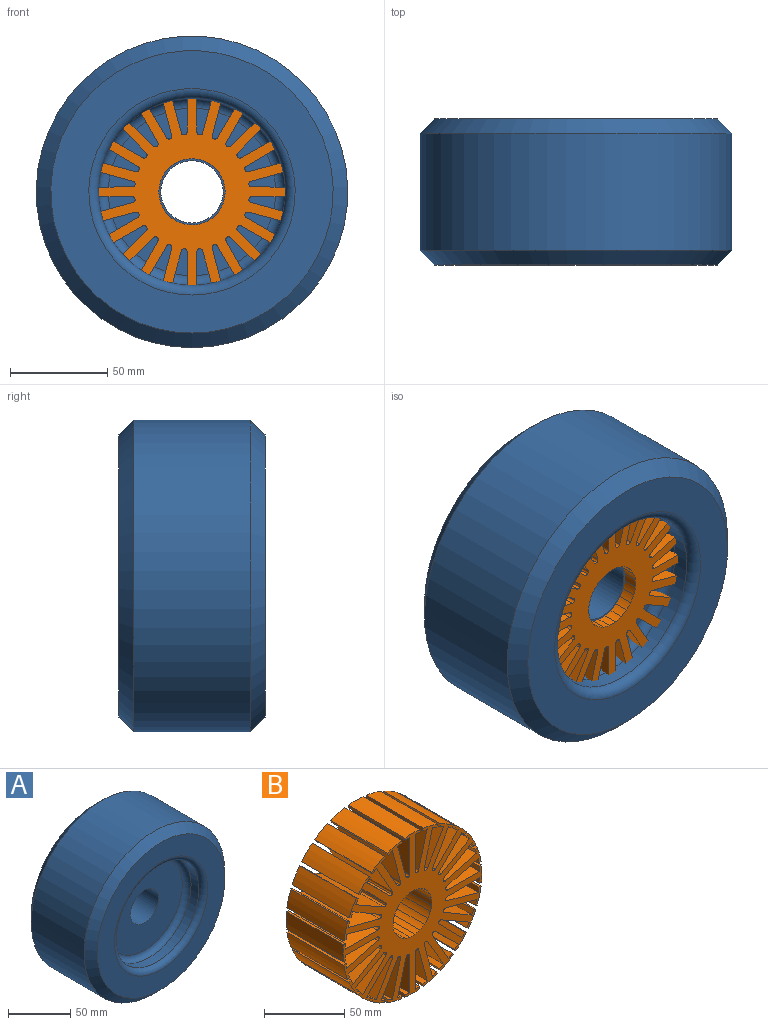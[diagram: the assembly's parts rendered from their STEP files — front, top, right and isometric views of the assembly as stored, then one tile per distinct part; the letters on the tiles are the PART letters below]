
ASSEMBLY  parts=2 mates=1
PART A: 14 faces, bbox 160x75x160 mm
  f0: cylinder r=16mm len=37.5mm, axis (0,1,0), area 3769.9mm2, adj f1,f2
  f1: plane 86x86mm, normal (0,-1,0), area 5004.6mm2, adj f0,f10
  f2: plane 86x86mm, normal (0,1,0), area 5004.6mm2, adj f0,f13
  f3: cylinder r=48mm len=96mm, axis (0,1,0), area 2638.9mm2, adj f10,f12
  f4: cylinder r=48mm len=96mm, axis (0,1,0), area 2638.9mm2, adj f11,f13
  f5: cylinder r=80mm len=160mm, axis (0,1,0), area 30159.3mm2, adj f8,f9
  f6: plane 145x145mm, normal (0,-1,0), area 7688.3mm2, adj f8,f12
  f7: plane 145x145mm, normal (0,1,0), area 7688.3mm2, adj f9,f11
  f8: cone r=72.5mm half-angle=45deg, axis (0,1,0), area 5081.5mm2, adj f5,f6
  f9: cone r=80mm half-angle=45deg, axis (0,-1,0), area 5081.5mm2, adj f5,f7
  f10: torus R=43mm, axis (0,-1,0), area 2279mm2, adj f1,f3
  f11: torus R=53mm, axis (0,-1,0), area 2458.4mm2, adj f4,f7
  f12: torus R=53mm, axis (0,-1,0), area 2458.4mm2, adj f3,f6
  f13: torus R=43mm, axis (0,-1,0), area 2279mm2, adj f2,f4
PART B: 250 faces, bbox 122x50x122 mm
  f0: cylinder r=1.5mm len=50mm, axis (0,1,0), area 108.3mm2, adj f10,f12,f13,f150
  f1: cylinder r=17mm len=50mm, axis (0,1,0), area 222.5mm2, adj f11,f12,f13,f147
  f2: plane 50x0mm, normal (0.99,0,-0.13), area 0mm2, adj f3,f12,f13,f14
  f3: cylinder r=1.5mm len=50mm, axis (0,1,0), area 108.3mm2, adj f2,f4,f12,f13
  f4: plane 50x28.48mm, normal (1,0,0), area 1424.1mm2, adj f3,f5,f12,f13
  f5: plane 50x3.93mm, normal (-0.13,0,-0.99), area 198.3mm2, adj f4,f6,f12,f13
  f6: plane 50x1.98mm, normal (0.99,0,-0.13), area 100mm2, adj f5,f7,f12,f13
  f7: cylinder r=61.01mm len=50mm, axis (0,1,0), area 660.6mm2, adj f6,f8,f12,f13
  f8: plane 50x1.98mm, normal (-0.99,0,-0.13), area 100mm2, adj f7,f9,f12,f13
  f9: plane 50x3.93mm, normal (0.13,0,-0.99), area 198.2mm2, adj f8,f10,f12,f13
  f10: plane 50x28.48mm, normal (-1,0,0), area 1424.1mm2, adj f0,f9,f12,f13
  f11: plane 50x0mm, normal (-0.99,0,-0.13), area 0mm2, adj f1,f12,f13,f149
  f12: plane 122.03x122.03mm, normal (0,-1,0), area 5955.8mm2, adj f0,f1,f2,f3,f4,f5,f6,f7
  f13: plane 122.03x122.03mm, normal (0,1,0), area 5955.8mm2, adj f0,f1,f2,f3,f4,f5,f6,f7
  f14: cylinder r=1.5mm len=50mm, axis (0,1,0), area 108.3mm2, adj f2,f12,f13,f146
  f15: cylinder r=1.5mm len=50mm, axis (0,1,0), area 108.3mm2, adj f12,f13,f25,f28
  f16: cylinder r=17mm len=50mm, axis (0,1,0), area 222.5mm2, adj f12,f13,f26,f249
  f17: plane 50x0mm, normal (-0.92,0,0.38), area 0mm2, adj f12,f13,f18,f148
  f18: cylinder r=1.5mm len=50mm, axis (0,1,0), area 108.3mm2, adj f12,f13,f17,f19
  f19: plane 50x27.55mm, normal (-0.97,0,0.25), area 1424.1mm2, adj f12,f13,f18,f20
  f20: plane 50x3.66mm, normal (0.38,0,0.92), area 198.2mm2, adj f12,f13,f19,f21
  f21: plane 50x1.85mm, normal (-0.92,0,0.38), area 100mm2, adj f12,f13,f20,f22
  f22: cylinder r=61.01mm len=50mm, axis (0,1,0), area 660.6mm2, adj f12,f13,f21,f23
  f23: plane 50x1.98mm, normal (0.99,0,-0.13), area 100mm2, adj f12,f13,f22,f24
  f24: plane 50x3.93mm, normal (0.13,0,0.99), area 198.3mm2, adj f12,f13,f23,f25
  f25: plane 50x27.48mm, normal (0.96,0,-0.26), area 1424.1mm2, adj f12,f13,f15,f24
  f26: plane 50x0mm, normal (0.99,0,-0.13), area 0mm2, adj f12,f13,f16,f27
  f27: cylinder r=17mm len=50mm, axis (0,1,0), area 222.5mm2, adj f12,f13,f26,f38
  f28: plane 50x0mm, normal (-0.99,0,0.13), area 0mm2, adj f12,f13,f15,f29
  f29: cylinder r=1.5mm len=50mm, axis (0,1,0), area 108.3mm2, adj f12,f13,f28,f30
  f30: plane 50x28.48mm, normal (-1,0,0), area 1424.1mm2, adj f12,f13,f29,f31
  f31: plane 50x3.93mm, normal (0.13,0,0.99), area 198.3mm2, adj f12,f13,f30,f32
  f32: plane 50x1.98mm, normal (-0.99,0,0.13), area 100mm2, adj f12,f13,f31,f33
  f33: cylinder r=61.01mm len=50mm, axis (0,1,0), area 660.6mm2, adj f12,f13,f32,f34
  f34: plane 50x1.98mm, normal (0.99,0,0.13), area 100mm2, adj f12,f13,f33,f35
  f35: plane 50x3.93mm, normal (-0.13,0,0.99), area 198.3mm2, adj f12,f13,f34,f36
  f36: plane 50x28.48mm, normal (1,0,0), area 1424.1mm2, adj f12,f13,f35,f37
  f37: cylinder r=1.5mm len=50mm, axis (0,1,0), area 108.3mm2, adj f12,f13,f36,f39
  f38: cylinder r=17mm len=50mm, axis (0,1,0), area 222.5mm2, adj f12,f13,f27,f48
  f39: cylinder r=1.5mm len=50mm, axis (0,1,0), area 108.3mm2, adj f12,f13,f37,f40
  f40: plane 50x27.47mm, normal (-0.96,0,-0.26), area 1424.1mm2, adj f12,f13,f39,f41
  f41: plane 50x3.93mm, normal (-0.13,0,0.99), area 198.3mm2, adj f12,f13,f40,f42
  f42: plane 50x1.98mm, normal (-0.99,0,-0.13), area 100mm2, adj f12,f13,f41,f43
  f43: cylinder r=61.01mm len=50mm, axis (0,1,0), area 660.6mm2, adj f12,f13,f42,f44
  f44: plane 50x1.85mm, normal (0.92,0,0.38), area 100mm2, adj f12,f13,f43,f45
  f45: plane 50x3.66mm, normal (-0.38,0,0.92), area 198.3mm2, adj f12,f13,f44,f46
  f46: plane 50x27.55mm, normal (0.97,0,0.25), area 1424.1mm2, adj f12,f13,f45,f47
  f47: cylinder r=1.5mm len=50mm, axis (0,1,0), area 108.3mm2, adj f12,f13,f46,f49
  f48: cylinder r=17mm len=50mm, axis (0,1,0), area 222.5mm2, adj f12,f13,f38,f58
  f49: cylinder r=1.5mm len=50mm, axis (0,1,0), area 108.3mm2, adj f12,f13,f47,f50
  f50: plane 50x24.6mm, normal (-0.86,0,-0.5), area 1424.1mm2, adj f12,f13,f49,f51
  f51: plane 50x3.66mm, normal (-0.38,0,0.92), area 198.2mm2, adj f12,f13,f50,f52
  f52: plane 50x1.85mm, normal (-0.92,0,-0.38), area 100mm2, adj f12,f13,f51,f53
  f53: cylinder r=61.01mm len=50mm, axis (0,1,0), area 660.6mm2, adj f12,f13,f52,f54
  f54: plane 50x1.59mm, normal (0.79,0,0.61), area 100mm2, adj f12,f13,f53,f55
  f55: plane 50x3.15mm, normal (-0.61,0,0.79), area 198.2mm2, adj f12,f13,f54,f56
  f56: plane 50x24.74mm, normal (0.87,0,0.5), area 1424.1mm2, adj f12,f13,f55,f57
  f57: cylinder r=1.5mm len=50mm, axis (0,1,0), area 108.3mm2, adj f12,f13,f56,f59
  f58: cylinder r=17mm len=50mm, axis (0,1,0), area 222.5mm2, adj f12,f13,f48,f68
  f59: cylinder r=1.5mm len=50mm, axis (0,1,0), area 108.3mm2, adj f12,f13,f57,f60
  f60: plane 50x20.24mm, normal (-0.7,0,-0.71), area 1424.1mm2, adj f12,f13,f59,f61
  f61: plane 50x3.15mm, normal (-0.61,0,0.79), area 198.3mm2, adj f12,f13,f60,f62
  f62: plane 50x1.59mm, normal (-0.79,0,-0.61), area 100mm2, adj f12,f13,f61,f63
  f63: cylinder r=61.01mm len=50mm, axis (0,1,0), area 660.6mm2, adj f12,f13,f62,f64
  f64: plane 50x1.59mm, normal (0.61,0,0.79), area 100mm2, adj f12,f13,f63,f65
  f65: plane 50x3.15mm, normal (-0.79,0,0.61), area 198.2mm2, adj f12,f13,f64,f66
  f66: plane 50x20.24mm, normal (0.71,0,0.7), area 1424.1mm2, adj f12,f13,f65,f67
  f67: cylinder r=1.5mm len=50mm, axis (0,1,0), area 108.3mm2, adj f12,f13,f66,f69
  f68: cylinder r=17mm len=50mm, axis (0,1,0), area 222.5mm2, adj f12,f13,f58,f78
  f69: cylinder r=1.5mm len=50mm, axis (0,1,0), area 108.3mm2, adj f12,f13,f67,f70
  f70: plane 50x24.74mm, normal (-0.5,0,-0.87), area 1424.1mm2, adj f12,f13,f69,f71
  f71: plane 50x3.15mm, normal (-0.79,0,0.61), area 198.3mm2, adj f12,f13,f70,f72
  f72: plane 50x1.59mm, normal (-0.61,0,-0.79), area 100mm2, adj f12,f13,f71,f73
  f73: cylinder r=61.01mm len=50mm, axis (0,1,0), area 660.6mm2, adj f12,f13,f72,f74
  f74: plane 50x1.85mm, normal (0.38,0,0.92), area 100mm2, adj f12,f13,f73,f75
  f75: plane 50x3.66mm, normal (-0.92,0,0.38), area 198.2mm2, adj f12,f13,f74,f76
  f76: plane 50x24.6mm, normal (0.5,0,0.86), area 1424.1mm2, adj f12,f13,f75,f77
  f77: cylinder r=1.5mm len=50mm, axis (0,1,0), area 108.3mm2, adj f12,f13,f76,f79
  f78: cylinder r=17mm len=50mm, axis (0,1,0), area 222.5mm2, adj f12,f13,f68,f88
  f79: cylinder r=1.5mm len=50mm, axis (0,1,0), area 108.3mm2, adj f12,f13,f77,f80
  f80: plane 50x27.55mm, normal (-0.25,0,-0.97), area 1424.1mm2, adj f12,f13,f79,f81
  f81: plane 50x3.66mm, normal (-0.92,0,0.38), area 198.2mm2, adj f12,f13,f80,f82
  f82: plane 50x1.85mm, normal (-0.38,0,-0.92), area 100mm2, adj f12,f13,f81,f83
  f83: cylinder r=61.01mm len=50mm, axis (0,1,0), area 660.6mm2, adj f12,f13,f82,f84
  f84: plane 50x1.98mm, normal (0.13,0,0.99), area 100mm2, adj f12,f13,f83,f85
  f85: plane 50x3.93mm, normal (-0.99,0,0.13), area 198.2mm2, adj f12,f13,f84,f86
  f86: plane 50x27.48mm, normal (0.26,0,0.96), area 1424.1mm2, adj f12,f13,f85,f87
  f87: cylinder r=1.5mm len=50mm, axis (0,1,0), area 108.3mm2, adj f12,f13,f86,f89
  f88: cylinder r=17mm len=50mm, axis (0,1,0), area 222.5mm2, adj f12,f13,f78,f98
  f89: cylinder r=1.5mm len=50mm, axis (0,1,0), area 108.3mm2, adj f12,f13,f87,f90
  f90: plane 50x28.48mm, normal (0,0,-1), area 1424.1mm2, adj f12,f13,f89,f91
  f91: plane 50x3.93mm, normal (-0.99,0,0.13), area 198.3mm2, adj f12,f13,f90,f92
  f92: plane 50x1.98mm, normal (-0.13,0,-0.99), area 100mm2, adj f12,f13,f91,f93
  f93: cylinder r=61.01mm len=50mm, axis (0,1,0), area 660.6mm2, adj f12,f13,f92,f94
  f94: plane 50x1.98mm, normal (-0.13,0,0.99), area 100mm2, adj f12,f13,f93,f95
  f95: plane 50x3.93mm, normal (-0.99,0,-0.13), area 198.3mm2, adj f12,f13,f94,f96
  f96: plane 50x28.48mm, normal (0,0,1), area 1424.1mm2, adj f12,f13,f95,f97
  f97: cylinder r=1.5mm len=50mm, axis (0,1,0), area 108.3mm2, adj f12,f13,f96,f99
  f98: cylinder r=17mm len=50mm, axis (0,1,0), area 222.5mm2, adj f12,f13,f88,f108
  f99: cylinder r=1.5mm len=50mm, axis (0,1,0), area 108.3mm2, adj f12,f13,f97,f100
  f100: plane 50x27.47mm, normal (0.26,0,-0.96), area 1424.1mm2, adj f12,f13,f99,f101
  f101: plane 50x3.93mm, normal (-0.99,0,-0.13), area 198.2mm2, adj f12,f13,f100,f102
  f102: plane 50x1.98mm, normal (0.13,0,-0.99), area 100mm2, adj f12,f13,f101,f103
  f103: cylinder r=61.01mm len=50mm, axis (0,1,0), area 660.6mm2, adj f12,f13,f102,f104
  f104: plane 50x1.85mm, normal (-0.38,0,0.92), area 100mm2, adj f12,f13,f103,f105
  f105: plane 50x3.66mm, normal (-0.92,0,-0.38), area 198.3mm2, adj f12,f13,f104,f106
  f106: plane 50x27.55mm, normal (-0.25,0,0.97), area 1424.1mm2, adj f12,f13,f105,f107
  f107: cylinder r=1.5mm len=50mm, axis (0,1,0), area 108.3mm2, adj f12,f13,f106,f109
  f108: cylinder r=17mm len=50mm, axis (0,1,0), area 222.5mm2, adj f12,f13,f98,f118
  f109: cylinder r=1.5mm len=50mm, axis (0,1,0), area 108.3mm2, adj f12,f13,f107,f110
  f110: plane 50x24.6mm, normal (0.5,0,-0.86), area 1424.1mm2, adj f12,f13,f109,f111
  f111: plane 50x3.66mm, normal (-0.92,0,-0.38), area 198.3mm2, adj f12,f13,f110,f112
  f112: plane 50x1.85mm, normal (0.38,0,-0.92), area 100mm2, adj f12,f13,f111,f113
  f113: cylinder r=61.01mm len=50mm, axis (0,1,0), area 660.6mm2, adj f12,f13,f112,f114
  f114: plane 50x1.59mm, normal (-0.61,0,0.79), area 100mm2, adj f12,f13,f113,f115
  f115: plane 50x3.15mm, normal (-0.79,0,-0.61), area 198.2mm2, adj f12,f13,f114,f116
  f116: plane 50x24.74mm, normal (-0.5,0,0.87), area 1424.1mm2, adj f12,f13,f115,f117
  f117: cylinder r=1.5mm len=50mm, axis (0,1,0), area 108.3mm2, adj f12,f13,f116,f119
  f118: cylinder r=17mm len=50mm, axis (0,1,0), area 222.5mm2, adj f12,f13,f108,f128
  f119: cylinder r=1.5mm len=50mm, axis (0,1,0), area 108.3mm2, adj f12,f13,f117,f120
  f120: plane 50x20.24mm, normal (0.71,0,-0.7), area 1424.1mm2, adj f12,f13,f119,f121
  f121: plane 50x3.15mm, normal (-0.79,0,-0.61), area 198.3mm2, adj f12,f13,f120,f122
  f122: plane 50x1.59mm, normal (0.61,0,-0.79), area 100mm2, adj f12,f13,f121,f123
  f123: cylinder r=61.01mm len=50mm, axis (0,1,0), area 660.6mm2, adj f12,f13,f122,f124
  f124: plane 50x1.59mm, normal (-0.79,0,0.61), area 100mm2, adj f12,f13,f123,f125
  f125: plane 50x3.15mm, normal (-0.61,0,-0.79), area 198.2mm2, adj f12,f13,f124,f126
  f126: plane 50x20.24mm, normal (-0.7,0,0.71), area 1424.1mm2, adj f12,f13,f125,f127
  f127: cylinder r=1.5mm len=50mm, axis (0,1,0), area 108.3mm2, adj f12,f13,f126,f129
  f128: cylinder r=17mm len=50mm, axis (0,1,0), area 222.5mm2, adj f12,f13,f118,f138
  f129: cylinder r=1.5mm len=50mm, axis (0,1,0), area 108.3mm2, adj f12,f13,f127,f130
  f130: plane 50x24.74mm, normal (0.87,0,-0.5), area 1424.1mm2, adj f12,f13,f129,f131
  f131: plane 50x3.15mm, normal (-0.61,0,-0.79), area 198.2mm2, adj f12,f13,f130,f132
  f132: plane 50x1.59mm, normal (0.79,0,-0.61), area 100mm2, adj f12,f13,f131,f133
  f133: cylinder r=61.01mm len=50mm, axis (0,1,0), area 660.6mm2, adj f12,f13,f132,f134
  f134: plane 50x1.85mm, normal (-0.92,0,0.38), area 100mm2, adj f12,f13,f133,f135
  f135: plane 50x3.66mm, normal (-0.38,0,-0.92), area 198.2mm2, adj f12,f13,f134,f136
  f136: plane 50x24.6mm, normal (-0.86,0,0.5), area 1424.1mm2, adj f12,f13,f135,f137
  f137: cylinder r=1.5mm len=50mm, axis (0,1,0), area 108.3mm2, adj f12,f13,f136,f139
  f138: cylinder r=17mm len=50mm, axis (0,1,0), area 222.5mm2, adj f12,f13,f128,f147
  f139: cylinder r=1.5mm len=50mm, axis (0,1,0), area 108.3mm2, adj f12,f13,f137,f140
  f140: plane 50x27.55mm, normal (0.97,0,-0.25), area 1424.1mm2, adj f12,f13,f139,f141
  f141: plane 50x3.66mm, normal (-0.38,0,-0.92), area 198.3mm2, adj f12,f13,f140,f142
  f142: plane 50x1.85mm, normal (0.92,0,-0.38), area 100mm2, adj f12,f13,f141,f143
  f143: cylinder r=61.01mm len=50mm, axis (0,1,0), area 660.6mm2, adj f12,f13,f142,f144
  f144: plane 50x1.98mm, normal (-0.99,0,0.13), area 100mm2, adj f12,f13,f143,f145
  f145: plane 50x3.93mm, normal (-0.13,0,-0.99), area 198.3mm2, adj f12,f13,f144,f146
  f146: plane 50x27.48mm, normal (-0.96,0,0.26), area 1424.1mm2, adj f12,f13,f14,f145
  f147: plane 50x0mm, normal (-0.99,0,0.13), area 0mm2, adj f1,f12,f13,f138
  f148: cylinder r=1.5mm len=50mm, axis (0,1,0), area 108.3mm2, adj f12,f13,f17,f248
  f149: cylinder r=17mm len=50mm, axis (0,1,0), area 222.5mm2, adj f11,f12,f13,f170
  f150: plane 50x0mm, normal (0.99,0,0.13), area 0mm2, adj f0,f12,f13,f151
  f151: cylinder r=1.5mm len=50mm, axis (0,1,0), area 108.3mm2, adj f12,f13,f150,f152
  f152: plane 50x27.47mm, normal (0.96,0,0.26), area 1424.1mm2, adj f12,f13,f151,f153
  f153: plane 50x3.93mm, normal (0.13,0,-0.99), area 198.3mm2, adj f12,f13,f152,f154
  f154: plane 50x1.98mm, normal (0.99,0,0.13), area 100mm2, adj f12,f13,f153,f155
  f155: cylinder r=61.01mm len=50mm, axis (0,1,0), area 660.6mm2, adj f12,f13,f154,f156
  f156: plane 50x1.85mm, normal (-0.92,0,-0.38), area 100mm2, adj f12,f13,f155,f157
  f157: plane 50x3.66mm, normal (0.38,0,-0.92), area 198.2mm2, adj f12,f13,f156,f158
  f158: plane 50x27.55mm, normal (-0.97,0,-0.25), area 1424.1mm2, adj f12,f13,f157,f159
  f159: cylinder r=1.5mm len=50mm, axis (0,1,0), area 108.3mm2, adj f12,f13,f158,f171
  f160: cylinder r=17mm len=50mm, axis (0,1,0), area 222.5mm2, adj f12,f13,f170,f180
  f161: cylinder r=1.5mm len=50mm, axis (0,1,0), area 108.3mm2, adj f12,f13,f162,f179
  f162: plane 50x20.24mm, normal (0.7,0,0.71), area 1424.1mm2, adj f12,f13,f161,f163
  f163: plane 50x3.15mm, normal (0.61,0,-0.79), area 198.2mm2, adj f12,f13,f162,f164
  f164: plane 50x1.59mm, normal (0.79,0,0.61), area 100mm2, adj f12,f13,f163,f165
  f165: cylinder r=61.01mm len=50mm, axis (0,1,0), area 660.6mm2, adj f12,f13,f164,f166
  f166: plane 50x1.59mm, normal (-0.61,0,-0.79), area 100mm2, adj f12,f13,f165,f167
  f167: plane 50x3.15mm, normal (0.79,0,-0.61), area 198.2mm2, adj f12,f13,f166,f168
  f168: plane 50x20.24mm, normal (-0.71,0,-0.7), area 1424.1mm2, adj f12,f13,f167,f169
  f169: cylinder r=1.5mm len=50mm, axis (0,1,0), area 108.3mm2, adj f12,f13,f168,f181
  f170: cylinder r=17mm len=50mm, axis (0,1,0), area 222.5mm2, adj f12,f13,f149,f160
  f171: cylinder r=1.5mm len=50mm, axis (0,1,0), area 108.3mm2, adj f12,f13,f159,f172
  f172: plane 50x24.6mm, normal (0.86,0,0.5), area 1424.1mm2, adj f12,f13,f171,f173
  f173: plane 50x3.66mm, normal (0.38,0,-0.92), area 198.3mm2, adj f12,f13,f172,f174
  f174: plane 50x1.85mm, normal (0.92,0,0.38), area 100mm2, adj f12,f13,f173,f175
  f175: cylinder r=61.01mm len=50mm, axis (0,1,0), area 660.6mm2, adj f12,f13,f174,f176
  f176: plane 50x1.59mm, normal (-0.79,0,-0.61), area 100mm2, adj f12,f13,f175,f177
  f177: plane 50x3.15mm, normal (0.61,0,-0.79), area 198.2mm2, adj f12,f13,f176,f178
  f178: plane 50x24.74mm, normal (-0.87,0,-0.5), area 1424.1mm2, adj f12,f13,f177,f179
  f179: cylinder r=1.5mm len=50mm, axis (0,1,0), area 108.3mm2, adj f12,f13,f161,f178
  f180: cylinder r=17mm len=50mm, axis (0,1,0), area 222.5mm2, adj f12,f13,f160,f190
  f181: cylinder r=1.5mm len=50mm, axis (0,1,0), area 108.3mm2, adj f12,f13,f169,f182
  f182: plane 50x24.74mm, normal (0.5,0,0.87), area 1424.1mm2, adj f12,f13,f181,f183
  f183: plane 50x3.15mm, normal (0.79,0,-0.61), area 198.2mm2, adj f12,f13,f182,f184
  f184: plane 50x1.59mm, normal (0.61,0,0.79), area 100mm2, adj f12,f13,f183,f185
  f185: cylinder r=61.01mm len=50mm, axis (0,1,0), area 660.6mm2, adj f12,f13,f184,f186
  f186: plane 50x1.85mm, normal (-0.38,0,-0.92), area 100mm2, adj f12,f13,f185,f187
  f187: plane 50x3.66mm, normal (0.92,0,-0.38), area 198.3mm2, adj f12,f13,f186,f188
  f188: plane 50x24.6mm, normal (-0.5,0,-0.86), area 1424.1mm2, adj f12,f13,f187,f189
  f189: cylinder r=1.5mm len=50mm, axis (0,1,0), area 108.3mm2, adj f12,f13,f188,f191
  f190: cylinder r=17mm len=50mm, axis (0,1,0), area 222.5mm2, adj f12,f13,f180,f200
  f191: cylinder r=1.5mm len=50mm, axis (0,1,0), area 108.3mm2, adj f12,f13,f189,f192
  f192: plane 50x27.55mm, normal (0.25,0,0.97), area 1424.1mm2, adj f12,f13,f191,f193
  f193: plane 50x3.66mm, normal (0.92,0,-0.38), area 198.3mm2, adj f12,f13,f192,f194
  f194: plane 50x1.85mm, normal (0.38,0,0.92), area 100mm2, adj f12,f13,f193,f195
  f195: cylinder r=61.01mm len=50mm, axis (0,1,0), area 660.6mm2, adj f12,f13,f194,f196
  f196: plane 50x1.98mm, normal (-0.13,0,-0.99), area 100mm2, adj f12,f13,f195,f197
  f197: plane 50x3.93mm, normal (0.99,0,-0.13), area 198.3mm2, adj f12,f13,f196,f198
  f198: plane 50x27.48mm, normal (-0.26,0,-0.96), area 1424.1mm2, adj f12,f13,f197,f199
  f199: cylinder r=1.5mm len=50mm, axis (0,1,0), area 108.3mm2, adj f12,f13,f198,f201
  f200: cylinder r=17mm len=50mm, axis (0,1,0), area 222.5mm2, adj f12,f13,f190,f210
  f201: cylinder r=1.5mm len=50mm, axis (0,1,0), area 108.3mm2, adj f12,f13,f199,f202
  f202: plane 50x28.48mm, normal (0,0,1), area 1424.1mm2, adj f12,f13,f201,f203
  f203: plane 50x3.93mm, normal (0.99,0,-0.13), area 198.3mm2, adj f12,f13,f202,f204
  f204: plane 50x1.98mm, normal (0.13,0,0.99), area 100mm2, adj f12,f13,f203,f205
  f205: cylinder r=61.01mm len=50mm, axis (0,1,0), area 660.6mm2, adj f12,f13,f204,f206
  f206: plane 50x1.98mm, normal (0.13,0,-0.99), area 100mm2, adj f12,f13,f205,f207
  f207: plane 50x3.93mm, normal (0.99,0,0.13), area 198.3mm2, adj f12,f13,f206,f208
  f208: plane 50x28.48mm, normal (0,0,-1), area 1424.1mm2, adj f12,f13,f207,f209
  f209: cylinder r=1.5mm len=50mm, axis (0,1,0), area 108.3mm2, adj f12,f13,f208,f211
  f210: cylinder r=17mm len=50mm, axis (0,1,0), area 222.5mm2, adj f12,f13,f200,f220
  f211: cylinder r=1.5mm len=50mm, axis (0,1,0), area 108.3mm2, adj f12,f13,f209,f212
  f212: plane 50x27.47mm, normal (-0.26,0,0.96), area 1424.1mm2, adj f12,f13,f211,f213
  f213: plane 50x3.93mm, normal (0.99,0,0.13), area 198.3mm2, adj f12,f13,f212,f214
  f214: plane 50x1.98mm, normal (-0.13,0,0.99), area 100mm2, adj f12,f13,f213,f215
  f215: cylinder r=61.01mm len=50mm, axis (0,1,0), area 660.6mm2, adj f12,f13,f214,f216
  f216: plane 50x1.85mm, normal (0.38,0,-0.92), area 100mm2, adj f12,f13,f215,f217
  f217: plane 50x3.66mm, normal (0.92,0,0.38), area 198.2mm2, adj f12,f13,f216,f218
  f218: plane 50x27.55mm, normal (0.25,0,-0.97), area 1424.1mm2, adj f12,f13,f217,f219
  f219: cylinder r=1.5mm len=50mm, axis (0,1,0), area 108.3mm2, adj f12,f13,f218,f221
  f220: cylinder r=17mm len=50mm, axis (0,1,0), area 222.5mm2, adj f12,f13,f210,f230
  f221: cylinder r=1.5mm len=50mm, axis (0,1,0), area 108.3mm2, adj f12,f13,f219,f222
  f222: plane 50x24.6mm, normal (-0.5,0,0.86), area 1424.1mm2, adj f12,f13,f221,f223
  f223: plane 50x3.66mm, normal (0.92,0,0.38), area 198.2mm2, adj f12,f13,f222,f224
  f224: plane 50x1.85mm, normal (-0.38,0,0.92), area 100mm2, adj f12,f13,f223,f225
  f225: cylinder r=61.01mm len=50mm, axis (0,1,0), area 660.6mm2, adj f12,f13,f224,f226
  f226: plane 50x1.59mm, normal (0.61,0,-0.79), area 100mm2, adj f12,f13,f225,f227
  f227: plane 50x3.15mm, normal (0.79,0,0.61), area 198.2mm2, adj f12,f13,f226,f228
  f228: plane 50x24.74mm, normal (0.5,0,-0.87), area 1424.1mm2, adj f12,f13,f227,f229
  f229: cylinder r=1.5mm len=50mm, axis (0,1,0), area 108.3mm2, adj f12,f13,f228,f231
  f230: cylinder r=17mm len=50mm, axis (0,1,0), area 222.5mm2, adj f12,f13,f220,f240
  f231: cylinder r=1.5mm len=50mm, axis (0,1,0), area 108.3mm2, adj f12,f13,f229,f232
  f232: plane 50x20.24mm, normal (-0.71,0,0.7), area 1424.1mm2, adj f12,f13,f231,f233
  f233: plane 50x3.15mm, normal (0.79,0,0.61), area 198.2mm2, adj f12,f13,f232,f234
  f234: plane 50x1.59mm, normal (-0.61,0,0.79), area 100mm2, adj f12,f13,f233,f235
  f235: cylinder r=61.01mm len=50mm, axis (0,1,0), area 660.6mm2, adj f12,f13,f234,f236
  f236: plane 50x1.59mm, normal (0.79,0,-0.61), area 100mm2, adj f12,f13,f235,f237
  f237: plane 50x3.15mm, normal (0.61,0,0.79), area 198.2mm2, adj f12,f13,f236,f238
  f238: plane 50x20.24mm, normal (0.7,0,-0.71), area 1424.1mm2, adj f12,f13,f237,f239
  f239: cylinder r=1.5mm len=50mm, axis (0,1,0), area 108.3mm2, adj f12,f13,f238,f241
  f240: cylinder r=17mm len=50mm, axis (0,1,0), area 222.5mm2, adj f12,f13,f230,f249
  f241: cylinder r=1.5mm len=50mm, axis (0,1,0), area 108.3mm2, adj f12,f13,f239,f242
  f242: plane 50x24.74mm, normal (-0.87,0,0.5), area 1424.1mm2, adj f12,f13,f241,f243
  f243: plane 50x3.15mm, normal (0.61,0,0.79), area 198.3mm2, adj f12,f13,f242,f244
  f244: plane 50x1.59mm, normal (-0.79,0,0.61), area 100mm2, adj f12,f13,f243,f245
  f245: cylinder r=61.01mm len=50mm, axis (0,1,0), area 660.6mm2, adj f12,f13,f244,f246
  f246: plane 50x1.85mm, normal (0.92,0,-0.38), area 100mm2, adj f12,f13,f245,f247
  f247: plane 50x3.66mm, normal (0.38,0,0.92), area 198.2mm2, adj f12,f13,f246,f248
  f248: plane 50x24.6mm, normal (0.86,0,-0.5), area 1424.1mm2, adj f12,f13,f148,f247
  f249: plane 50x0mm, normal (0.92,0,-0.38), area 0mm2, adj f12,f13,f16,f240
PLACE A t=(-42.94,-4.19,31.18)mm
PLACE B t=(-42.61,-5.44,31.16)mm
MATE fastened B.f7 <-> A.f0  axis (0,1,0) through (-42.94,19.56,31.18)mm
